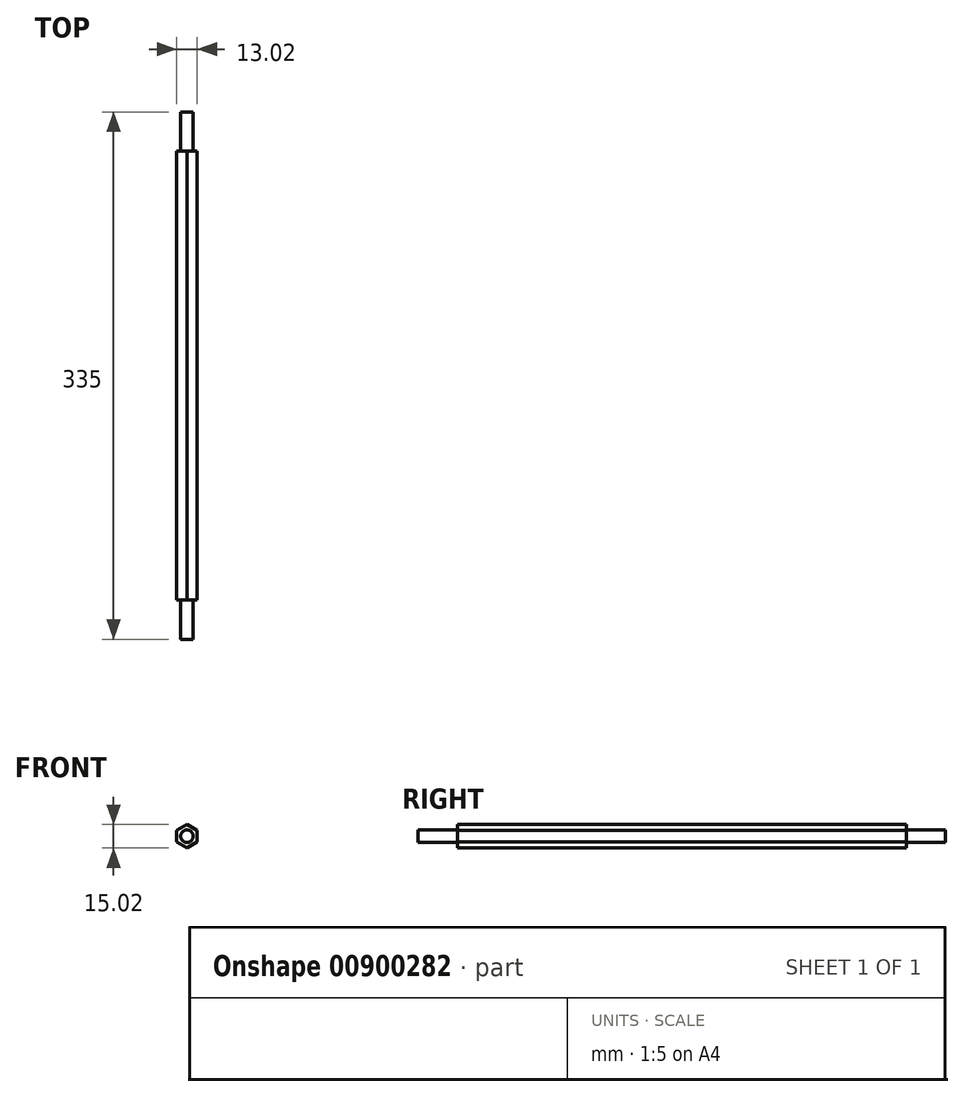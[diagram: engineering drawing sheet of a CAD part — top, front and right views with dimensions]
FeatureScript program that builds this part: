
annotation { "Feature Type Name" : "Feature", "Feature Type Description" : "" }
export const myFeature = defineFeature(function(context is Context, id is Id, definition is map)
    precondition{}
    {
        {
            var Q0;
            Q0=qCreatedBy(makeId("Front.planeOp"),FACE);
            var sketch = newSketch(context, id + "F0", { "sketchPlane" : qUnion([Q0])});
            skCircle(sketch, "E0.cCircle", {"center": v(0, 0) * mm, "radius": 6.5 * mm, "construction": true});
            skLineSegment(sketch, "E0.0", {"start": v(6.51, -3.74) * mm, "end": v(0.02, -7.5) * mm});
            skLineSegment(sketch, "E0.1", {"start": v(0.02, -7.5) * mm, "end": v(-6.49, -3.77) * mm});
            skLineSegment(sketch, "E0.2", {"start": v(-6.49, -3.77) * mm, "end": v(-6.51, 3.74) * mm});
            skLineSegment(sketch, "E0.3", {"start": v(-6.51, 3.74) * mm, "end": v(-0.02, 7.5) * mm});
            skLineSegment(sketch, "E0.4", {"start": v(-0.02, 7.5) * mm, "end": v(6.49, 3.77) * mm});
            skLineSegment(sketch, "E0.5", {"start": v(6.49, 3.77) * mm, "end": v(6.51, -3.74) * mm});
            skPoint(sketch, "E0.0.midPoint", {"position": v(3.27, -5.62) * mm});
            skSolve(sketch);
        }
        {
            var Q0;
            Q0 = qSketchRegion(id + "F0", true);
            extrude(context, id + "F1", {"entities" : qUnion([Q0]), "depth" : 285 * mm, "offsetDistance" : 25 * mm});
        }
        {
            var Q0;
            Q0=makeQuery(id+"F1.opExtrude","CAP_FACE",FACE,{"disambiguationData":[OSD([sQuery(id+"F0.wireOp",EDGE,"E0.0"),sQuery(id+"F0.wireOp",EDGE,"E0.1"),sQuery(id+"F0.wireOp",EDGE,"E0.2"),sQuery(id+"F0.wireOp",EDGE,"E0.3"),sQuery(id+"F0.wireOp",EDGE,"E0.4"),sQuery(id+"F0.wireOp",EDGE,"E0.5")])],"isStart":true});
            var sketch = newSketch(context, id + "F2", { "sketchPlane" : qUnion([Q0])});
            skCircle(sketch, "E1", {"center": v(0, 0) * mm, "radius": 4 * mm});
            skSolve(sketch);
        }
        {
            var Q0;
            Q0 = qSketchRegion(id + "F2", true);
            extrude(context, id + "F3", {"entities" : qUnion([Q0]), "operationType" : NewBodyOperationType.ADD, "depth" : 25 * mm, "offsetDistance" : 25 * mm});
        }
        {
            var Q0;
            Q0=makeQuery(id+"F1.opExtrude","CAP_FACE",FACE,{"disambiguationData":[OSD([sQuery(id+"F0.wireOp",EDGE,"E0.0"),sQuery(id+"F0.wireOp",EDGE,"E0.1"),sQuery(id+"F0.wireOp",EDGE,"E0.2"),sQuery(id+"F0.wireOp",EDGE,"E0.3"),sQuery(id+"F0.wireOp",EDGE,"E0.4"),sQuery(id+"F0.wireOp",EDGE,"E0.5")])],"isStart":false});
            var sketch = newSketch(context, id + "F4", { "sketchPlane" : qUnion([Q0])});
            skCircle(sketch, "E2", {"center": v(0, 0) * mm, "radius": 4 * mm});
            skSolve(sketch);
        }
        {
            var Q0;
            Q0 = qSketchRegion(id + "F4", true);
            extrude(context, id + "F5", {"entities" : qUnion([Q0]), "operationType" : NewBodyOperationType.ADD, "depth" : 25 * mm, "offsetDistance" : 25 * mm});
        }
    });
